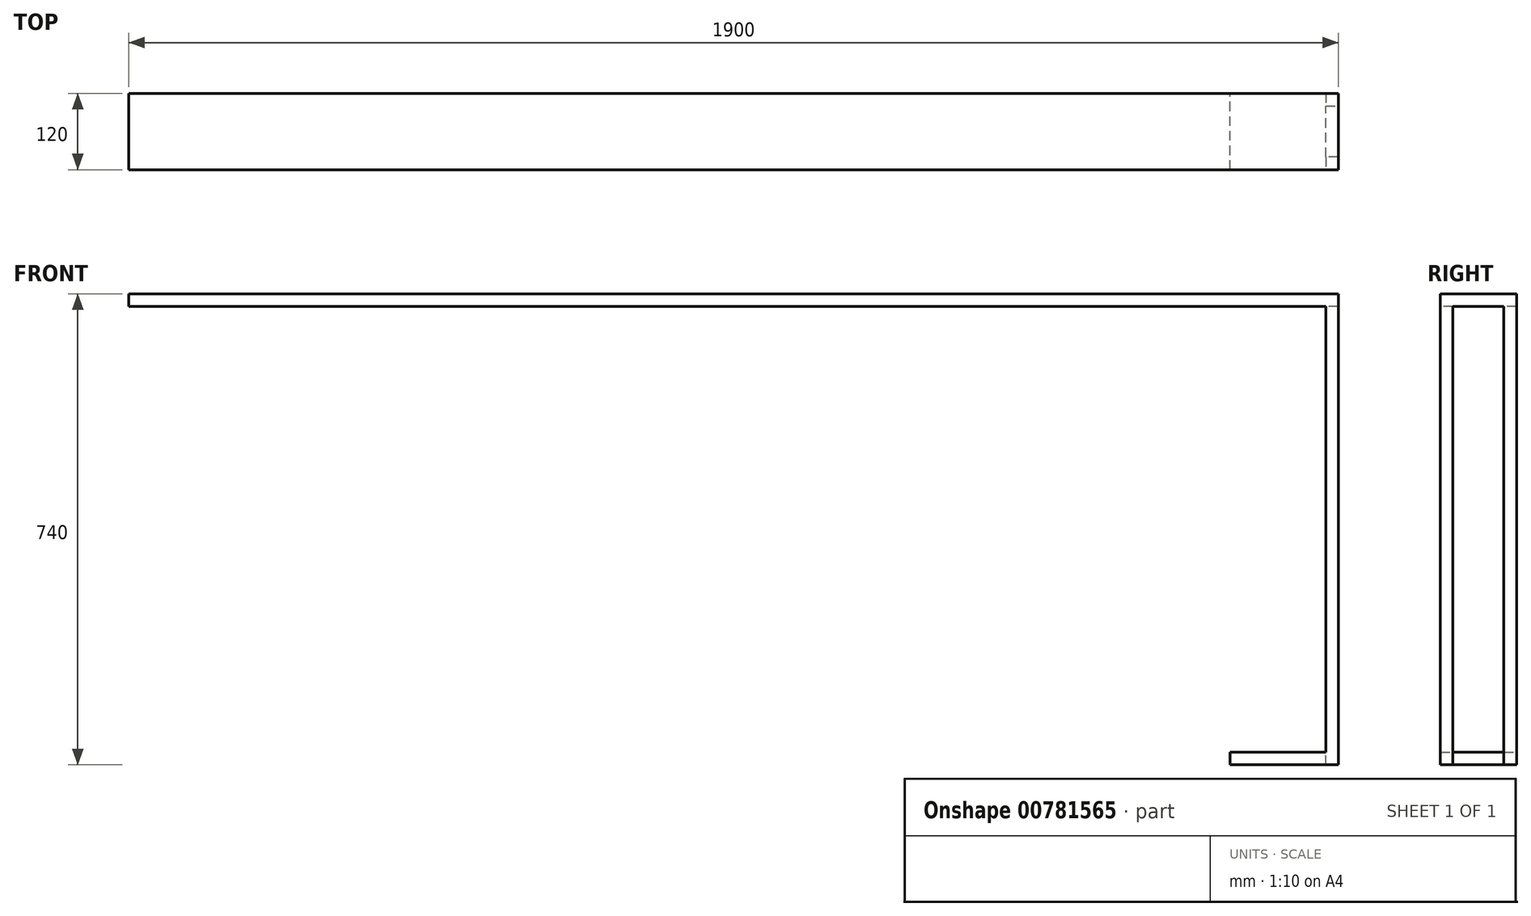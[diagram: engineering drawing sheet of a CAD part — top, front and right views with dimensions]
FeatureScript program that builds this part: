
annotation { "Feature Type Name" : "Feature", "Feature Type Description" : "" }
export const myFeature = defineFeature(function(context is Context, id is Id, definition is map)
    precondition{}
    {
        {
            var Q0;
            Q0=qCreatedBy(makeId("Top.planeOp"),FACE);
            var sketch = newSketch(context, id + "F0", { "sketchPlane" : qUnion([Q0])});
            skLineSegment(sketch, "E0", {"start": v(0, 0) * mm, "end": v(1900, 0) * mm});
            skLineSegment(sketch, "E1", {"start": v(1900, 120) * mm, "end": v(0, 120) * mm});
            skLineSegment(sketch, "E2", {"start": v(0, 120) * mm, "end": v(0, 0) * mm});
            skLineSegment(sketch, "E3", {"start": v(1900, 120) * mm, "end": v(1900, 0) * mm});
            skSolve(sketch);
        }
        {
            var Q0;
            Q0 = qSketchRegion(id + "F0", true);
            extrude(context, id + "F1", {"entities" : qUnion([Q0]), "oppositeDirection" : true, "depth" : 20 * mm, "offsetDistance" : 25 * mm});
        }
        {
            var Q0;
            Q0=makeQuery(id+"F1.opExtrude","CAP_FACE",FACE,{"disambiguationData":[OSD([sQuery(id+"F0.wireOp",EDGE,"E0"),sQuery(id+"F0.wireOp",EDGE,"E1"),sQuery(id+"F0.wireOp",EDGE,"E2"),sQuery(id+"F0.wireOp",EDGE,"E3")])],"isStart":false});
            var sketch = newSketch(context, id + "F2", { "sketchPlane" : qUnion([Q0])});
            skLineSegment(sketch, "E4", {"start": v(1900, -120) * mm, "end": v(1880, -120) * mm});
            skLineSegment(sketch, "E5", {"start": v(1880, -120) * mm, "end": v(1880, -100) * mm});
            skLineSegment(sketch, "E6", {"start": v(1880, -100) * mm, "end": v(1900, -100) * mm});
            skLineSegment(sketch, "E7", {"start": v(1900, -100) * mm, "end": v(1900, -120) * mm});
            skLineSegment(sketch, "E8", {"start": v(1900, -20) * mm, "end": v(1880, -20) * mm});
            skLineSegment(sketch, "E9", {"start": v(1880, -20) * mm, "end": v(1880, 0) * mm});
            skLineSegment(sketch, "E10", {"start": v(1880, 0) * mm, "end": v(1900, 0) * mm});
            skLineSegment(sketch, "E11", {"start": v(1900, 0) * mm, "end": v(1900, -20) * mm});
            skSolve(sketch);
        }
        {
            var Q0;
            Q0 = qSketchRegion(id + "F2", true);
            extrude(context, id + "F3", {"entities" : qUnion([Q0]), "operationType" : NewBodyOperationType.ADD, "depth" : 720 * mm, "offsetDistance" : 25 * mm});
        }
        {
            var Q0;
            Q0=makeQuery(id+"F3.boolean.opBoolean","MERGE",FACE,{"derivedFrom":[makeQuery(id+"F1.opExtrude","SWEPT_FACE",FACE,{"disambiguationData":[OSD([sQuery(id+"F0.wireOp",EDGE,"E1")])]}),makeQuery(id+"F3.opExtrude","SWEPT_FACE",FACE,{"disambiguationData":[OSD([sQuery(id+"F2.wireOp",EDGE,"E4")])]})]});
            var sketch = newSketch(context, id + "F4", { "sketchPlane" : qUnion([Q0])});
            skLineSegment(sketch, "E12", {"start": v(-1880, -740) * mm, "end": v(-1730, -740) * mm});
            skLineSegment(sketch, "E13", {"start": v(-1730, -740) * mm, "end": v(-1730, -720) * mm});
            skLineSegment(sketch, "E14", {"start": v(-1730, -720) * mm, "end": v(-1880, -720) * mm});
            skLineSegment(sketch, "E15", {"start": v(-1880, -720) * mm, "end": v(-1880, -740) * mm});
            skSolve(sketch);
        }
        {
            var Q0;
            Q0 = qSketchRegion(id + "F4", true);
            extrude(context, id + "F5", {"entities" : qUnion([Q0]), "operationType" : NewBodyOperationType.ADD, "oppositeDirection" : true, "depth" : 120 * mm, "offsetDistance" : 25 * mm});
        }
    });
